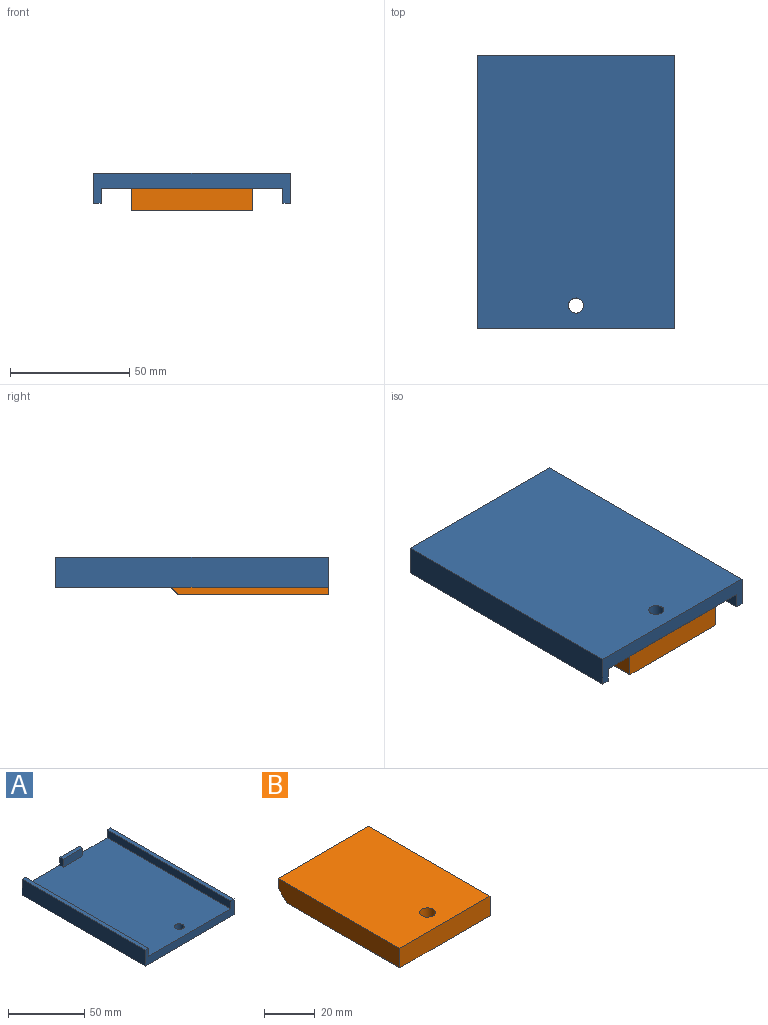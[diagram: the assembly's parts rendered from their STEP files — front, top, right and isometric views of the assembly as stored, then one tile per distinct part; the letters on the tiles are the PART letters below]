
ASSEMBLY  parts=2 mates=1
PART A: 15 faces, bbox 82.6x114.3x12.7 mm
  f0: plane 114.3x76.2mm, normal (0,0,1), area 8620.4mm2, adj f1,f3,f5,f7,f9,f11,f12,f13
  f1: plane 82.55x12.7mm, normal (0,1,0), area 679.7mm2, adj f0,f2,f4,f6,f7,f8,f9,f10
  f2: plane 114.3x12.7mm, normal (-1,0,0), area 1451.6mm2, adj f1,f3,f6,f10
  f3: plane 82.55x12.7mm, normal (0,-1,0), area 564.5mm2, adj f0,f2,f4,f6,f7,f8,f9,f10
  f4: plane 114.3x12.7mm, normal (1,0,0), area 1451.6mm2, adj f1,f3,f6,f8
  f5: cylinder r=3.17mm len=6.35mm, axis (0,0,-1), area 126.7mm2, adj f0,f6
  f6: plane 114.3x82.55mm, normal (0,0,-1), area 9403.8mm2, adj f1,f2,f3,f4,f5
  f7: plane 114.3x6.35mm, normal (-1,0,0), area 725.8mm2, adj f0,f1,f3,f8
  f8: plane 114.3x3.18mm, normal (0,0,1), area 362.9mm2, adj f1,f3,f4,f7
  f9: plane 114.3x6.35mm, normal (1,0,0), area 725.8mm2, adj f0,f1,f3,f10
  f10: plane 114.3x3.18mm, normal (0,0,1), area 362.9mm2, adj f1,f2,f3,f9
  f11: plane 6.35x3.18mm, normal (-1,0,0), area 20.2mm2, adj f0,f1,f12,f14
  f12: plane 18.14x6.35mm, normal (0,-1,0), area 115.2mm2, adj f0,f11,f13,f14
  f13: plane 6.35x3.18mm, normal (1,0,0), area 20.2mm2, adj f0,f1,f12,f14
  f14: plane 18.14x3.18mm, normal (0,0,1), area 57.6mm2, adj f1,f11,f12,f13
PART B: 10 faces, bbox 50.8x67.9x9.5 mm
  f0: plane 67.95x9.27mm, normal (-1,0,0), area 618.3mm2, adj f1,f3,f5,f7,f9
  f1: plane 50.8x9.53mm, normal (0,-1,0), area 483.8mm2, adj f0,f2,f5,f6,f8,f9
  f2: plane 67.95x9.27mm, normal (1,0,0), area 618.3mm2, adj f1,f3,f5,f7,f8
  f3: plane 50.8x4.45mm, normal (0,1,0), area 225.8mm2, adj f0,f2,f5,f7
  f4: cylinder r=3.17mm len=9.53mm, axis (0,0,-1), area 190mm2, adj f5,f6
  f5: plane 67.95x50.8mm, normal (0,0,1), area 3419.9mm2, adj f0,f1,f2,f3,f4
  f6: plane 62.87x50.29mm, normal (0,0,-1), area 3129.9mm2, adj f1,f4,f7,f8,f9
  f7: plane 50.8x5.08mm, normal (0,0.71,-0.71), area 364.9mm2, adj f0,f2,f3,f6,f8,f9
  f8: plane 63.12x0.25mm, normal (0.71,0,-0.71), area 22.6mm2, adj f1,f2,f6,f7
  f9: plane 63.12x0.25mm, normal (-0.71,0,-0.71), area 22.6mm2, adj f0,f1,f6,f7
PLACE A rot(axis=(0,1,0),180deg) t=(73.54,-1.97,31.18)mm
PLACE B t=(6.87,-1.97,15.3)mm
MATE fastened A.f5 <-> B.f4  axis (0,0,-1) through (32.27,7.56,24.83)mm
